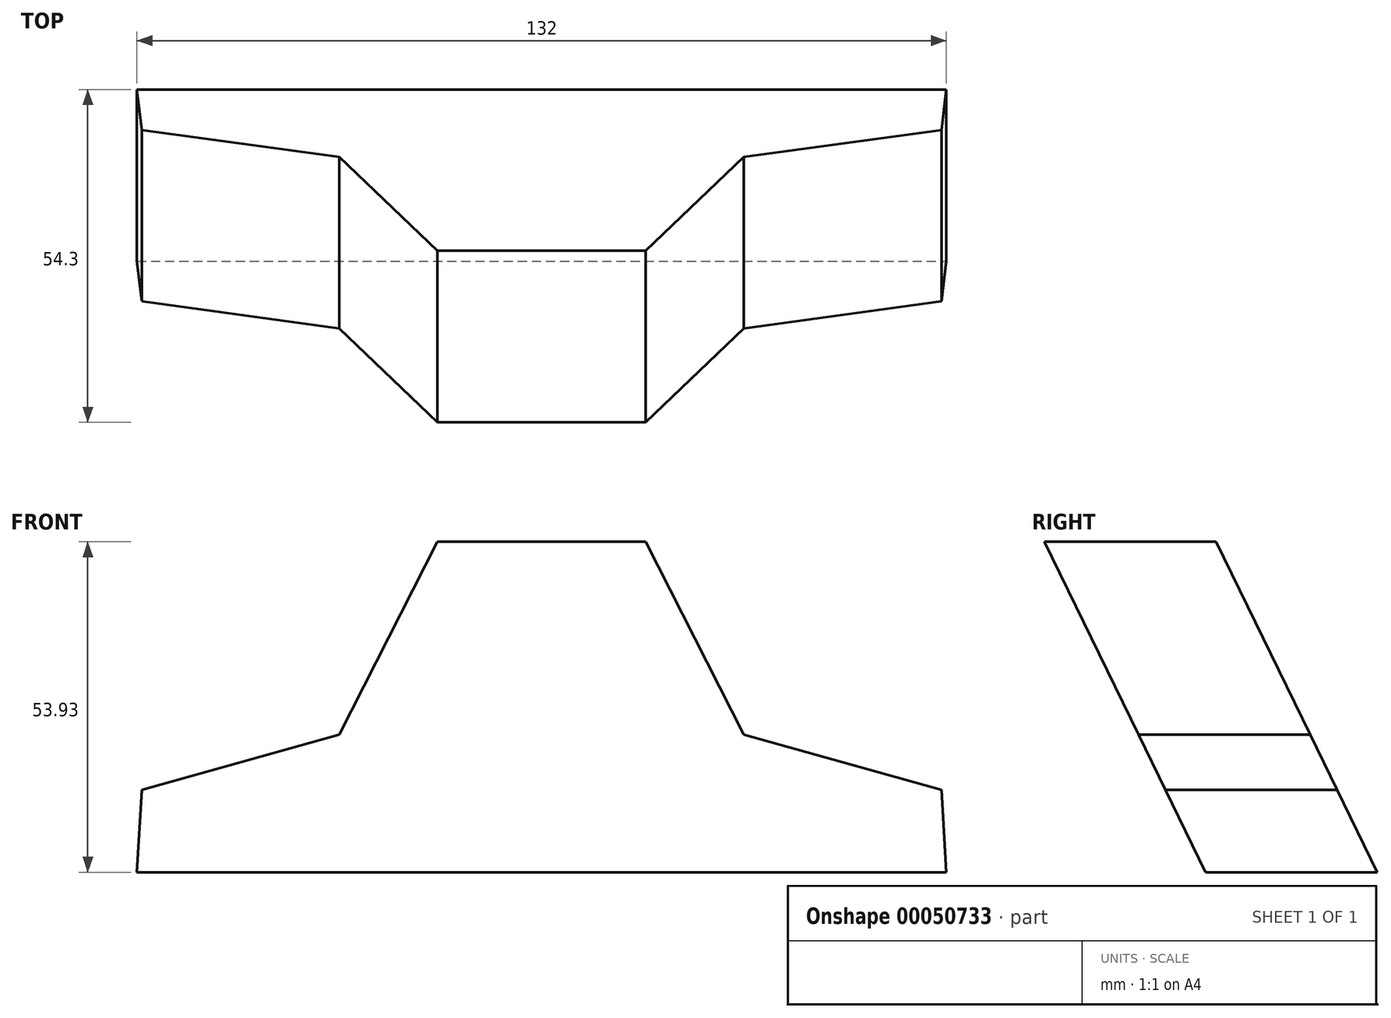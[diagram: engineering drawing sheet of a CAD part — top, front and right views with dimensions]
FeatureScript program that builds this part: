
annotation { "Feature Type Name" : "Feature", "Feature Type Description" : "" }
export const myFeature = defineFeature(function(context is Context, id is Id, definition is map)
    precondition{}
    {
        {
            var Q0;
            Q0=qCreatedBy(makeId("Front.planeOp"),FACE);
            var sketch = newSketch(context, id + "F0", { "sketchPlane" : qUnion([Q0])});
            skLineSegment(sketch, "E0", {"start": v(-38.92, 0) * mm, "end": v(36.33, 0) * mm, "construction": true});
            skSolve(sketch);
        }
        {
            var Q0;
            Q0=sQuery(id+"F0.wireOp",EDGE,"E0");
            cPlane(context, id + "F1", {"entities" : qUnion([Q0]), "cplaneType" : CPlaneType.LINE_ANGLE, "offset" : 150 * mm, "angle" : 26 * degree, "width" : 150 * mm, "height" : 150 * mm});
        }
        {
            var Q0;
            Q0=qCreatedBy(id+"F1.planeOp",FACE);
            var sketch = newSketch(context, id + "F2", { "sketchPlane" : qUnion([Q0])});
            skLineSegment(sketch, "E1", {"start": v(0, 133.09) * mm, "end": v(0, -42.77) * mm, "construction": true});
            skLineSegment(sketch, "E2", {"start": v(0, 0) * mm, "end": v(-66, 0) * mm});
            skLineSegment(sketch, "E3", {"start": v(-65.21, 14.98) * mm, "end": v(-33, 25) * mm});
            skLineSegment(sketch, "E4", {"start": v(-33, 25) * mm, "end": v(-17, 60) * mm});
            skLineSegment(sketch, "E5", {"start": v(-17, 60) * mm, "end": v(0, 60) * mm});
            skLineSegment(sketch, "E6", {"start": v(-66, 0) * mm, "end": v(-66, 52.38) * mm, "construction": true});
            skLineSegment(sketch, "E7", {"start": v(-66, 0) * mm, "end": v(-65.21, 14.98) * mm});
            skLineSegment(sketch, "E8.MirrorCS", {"start": v(0, 0) * mm, "end": v(66, 0) * mm});
            skLineSegment(sketch, "E9.MirrorCS", {"start": v(65.21, 14.98) * mm, "end": v(33, 25) * mm});
            skLineSegment(sketch, "E10.MirrorCS", {"start": v(33, 25) * mm, "end": v(17, 60) * mm});
            skLineSegment(sketch, "E11.MirrorCS", {"start": v(66, 0) * mm, "end": v(65.21, 14.98) * mm});
            skLineSegment(sketch, "E12.MirrorCS", {"start": v(66, 0) * mm, "end": v(66, 52.38) * mm, "construction": true});
            skLineSegment(sketch, "E13.MirrorCS", {"start": v(17, 60) * mm, "end": v(0, 60) * mm});
            skSolve(sketch);
        }
        {
            var Q0;
            Q0=qCreatedBy(makeId("Right.planeOp"),FACE);
            var sketch = newSketch(context, id + "F3", { "sketchPlane" : qUnion([Q0])});
            skLineSegment(sketch, "E14", {"start": v(0, 0) * mm, "end": v(-28, 0) * mm, "construction": true});
            skSolve(sketch);
        }
        {
            var Q0;
            Q0=sQuery(id+"F3.wireOp",VERTEX,"E14.end");
            var Q1;
            Q1=qCreatedBy(id+"F1.planeOp",FACE);
            cPlane(context, id + "F4", {"entities" : qUnion([Q0, Q1]), "cplaneType" : CPlaneType.PLANE_POINT, "offset" : 150 * mm, "width" : 150 * mm, "height" : 150 * mm});
        }
        {
            var Q0;
            Q0=qCreatedBy(id+"F4.planeOp",FACE);
            var sketch = newSketch(context, id + "F5", { "sketchPlane" : qUnion([Q0])});
            skLineSegment(sketch, "E15", {"start": v(0, 239.16) * mm, "end": v(0, 63.3) * mm, "construction": true});
            skLineSegment(sketch, "E16", {"start": v(0, 12.27) * mm, "end": v(-66, 12.27) * mm});
            skLineSegment(sketch, "E17", {"start": v(-65.21, 27.25) * mm, "end": v(-33, 37.27) * mm});
            skLineSegment(sketch, "E18", {"start": v(-33, 37.27) * mm, "end": v(-17, 72.27) * mm});
            skLineSegment(sketch, "E19", {"start": v(-66, 12.27) * mm, "end": v(-66, 158.45) * mm, "construction": true});
            skLineSegment(sketch, "E20", {"start": v(-66, 12.27) * mm, "end": v(-65.21, 27.25) * mm});
            skLineSegment(sketch, "E21.MirrorCS", {"start": v(0, 12.27) * mm, "end": v(66, 12.27) * mm});
            skLineSegment(sketch, "E22.MirrorCS", {"start": v(33, 37.27) * mm, "end": v(17, 72.27) * mm});
            skLineSegment(sketch, "E23.MirrorCS", {"start": v(66, 12.27) * mm, "end": v(65.21, 27.25) * mm});
            skLineSegment(sketch, "E24.MirrorCS", {"start": v(66, 12.27) * mm, "end": v(66, 158.45) * mm, "construction": true});
            skLineSegment(sketch, "E25", {"start": v(-17, 72.27) * mm, "end": v(0, 72.27) * mm});
            skLineSegment(sketch, "E26.MirrorCS", {"start": v(65.21, 27.25) * mm, "end": v(33, 37.27) * mm});
            skLineSegment(sketch, "E27.MirrorCS", {"start": v(17, 72.27) * mm, "end": v(0, 72.27) * mm});
            skSolve(sketch);
        }
        {
            var Q0;
            Q0=makeQuery(id+"F5.imprint","IMPRINT",FACE,{"disambiguationData":[TD([[makeQuery(id+"F5.imprint","IMPRINT",EDGE,{"derivedFrom":sQuery(id+"F5.wireOp",EDGE,"E16")}),-1.0]])]});
            var Q1;
            Q1=makeQuery(id+"F2.imprint","IMPRINT",FACE,{"disambiguationData":[TD([[makeQuery(id+"F2.imprint","IMPRINT",EDGE,{"derivedFrom":sQuery(id+"F2.wireOp",EDGE,"E2")}),-1.0]])]});
            loft(context, id + "F6", {"sheetProfilesArray" : [{ "sheetProfileEntities" : qUnion([Q0]) }, { "sheetProfileEntities" : qUnion([Q1]) }]});
        }
    });
